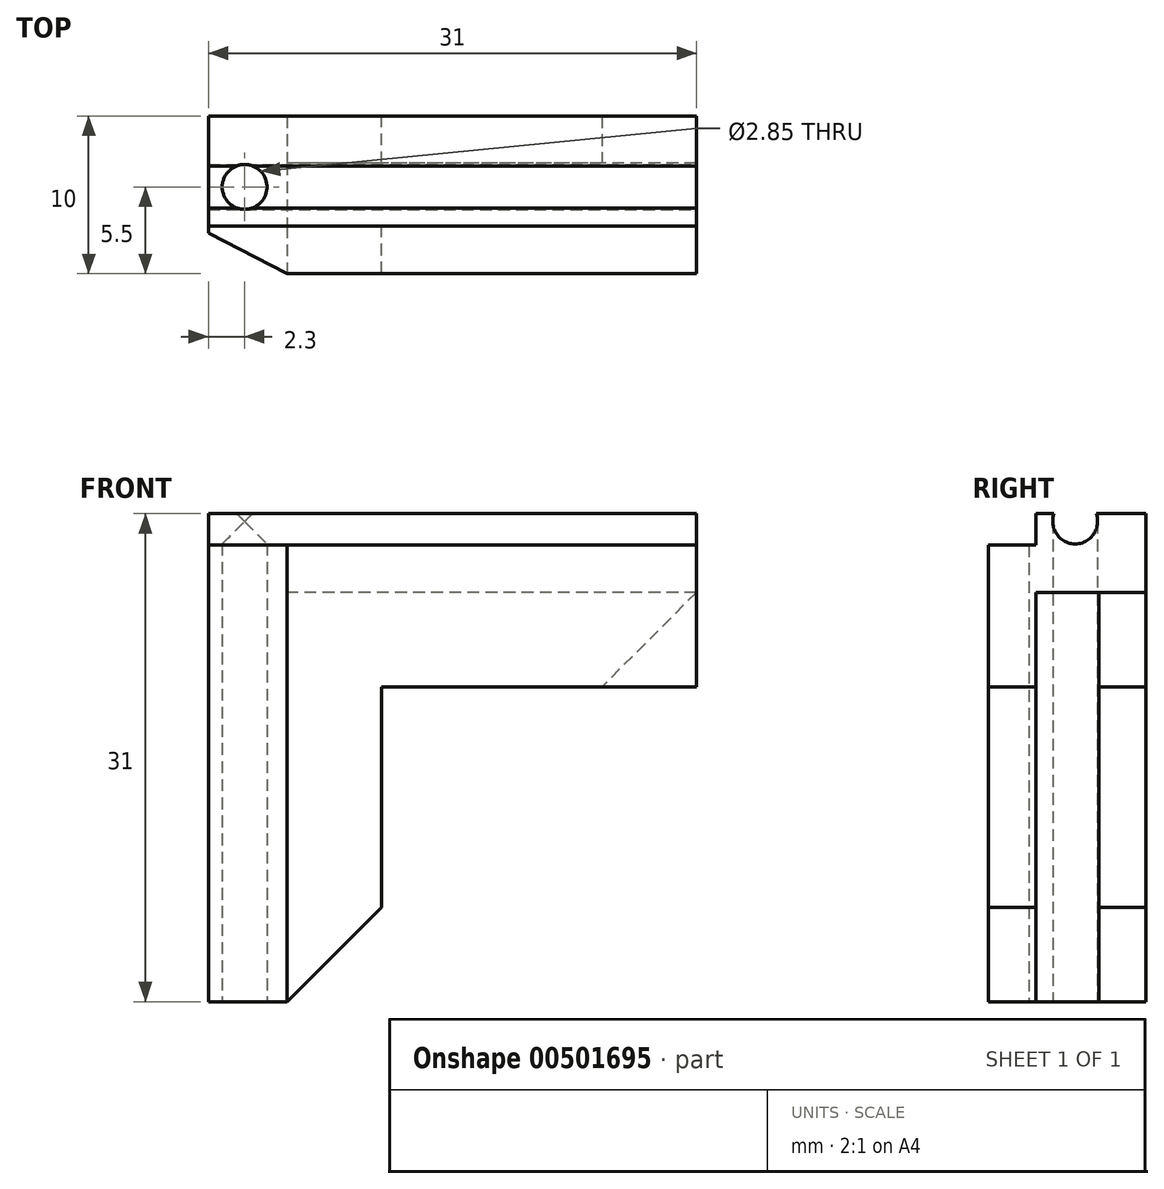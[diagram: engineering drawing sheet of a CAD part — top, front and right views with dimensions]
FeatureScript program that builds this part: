
annotation { "Feature Type Name" : "Feature", "Feature Type Description" : "" }
export const myFeature = defineFeature(function(context is Context, id is Id, definition is map)
    precondition{}
    {
        {
            var Q0;
            Q0=qCreatedBy(makeId("Top.planeOp"),FACE);
            var sketch = newSketch(context, id + "F0", { "sketchPlane" : qUnion([Q0])});
            skLineSegment(sketch, "E0", {"start": v(-12.16, 9.11) * mm, "end": v(-12.16, -0.89) * mm});
            skLineSegment(sketch, "E1", {"start": v(-12.16, -0.89) * mm, "end": v(-3.16, -0.89) * mm});
            skLineSegment(sketch, "E2", {"start": v(-3.16, -0.89) * mm, "end": v(-3.16, 2.11) * mm});
            skLineSegment(sketch, "E3", {"start": v(-3.16, 2.11) * mm, "end": v(-9.16, 2.11) * mm});
            skLineSegment(sketch, "E4", {"start": v(-9.16, 2.11) * mm, "end": v(-9.16, 6.11) * mm});
            skLineSegment(sketch, "E5", {"start": v(-9.16, 6.11) * mm, "end": v(-3.16, 6.11) * mm});
            skLineSegment(sketch, "E6", {"start": v(-3.16, 6.11) * mm, "end": v(-3.16, 9.11) * mm});
            skLineSegment(sketch, "E7", {"start": v(-3.16, 9.11) * mm, "end": v(-12.16, 9.11) * mm});
            skSolve(sketch);
        }
        {
            var Q0;
            Q0=makeQuery(id+"F0.imprint","IMPRINT",FACE,{"disambiguationData":[TD([[makeQuery(id+"F0.imprint","IMPRINT",EDGE,{"derivedFrom":sQuery(id+"F0.wireOp",EDGE,"E0")}),1.0]])]});
            extrude(context, id + "F1", {"entities" : qUnion([Q0]), "depth" : 20 * mm});
        }
        {
            var Q0;
            Q0=makeQuery(id+"F1.opExtrude","SWEPT_FACE",FACE,{"disambiguationData":[OSD([sQuery(id+"F0.wireOp",EDGE,"E0")])]});
            var sketch = newSketch(context, id + "F2", { "sketchPlane" : qUnion([Q0])});
            skLineSegment(sketch, "E8.bottom", {"start": v(-9.11, 20) * mm, "end": v(-2.11, 20) * mm});
            skLineSegment(sketch, "E8.top", {"start": v(-9.11, 0) * mm, "end": v(-2.11, 0) * mm});
            skLineSegment(sketch, "E8.left", {"start": v(-9.11, 20) * mm, "end": v(-9.11, 0) * mm});
            skLineSegment(sketch, "E8.right", {"start": v(-2.11, 20) * mm, "end": v(-2.11, 0) * mm});
            skSolve(sketch);
        }
        {
            var Q0;
            Q0=makeQuery(id+"F2.imprint","IMPRINT",FACE,{"disambiguationData":[TD([[makeQuery(id+"F2.imprint","IMPRINT",EDGE,{"derivedFrom":sQuery(id+"F2.wireOp",EDGE,"E8.bottom")}),-1.0]])]});
            extrude(context, id + "F3", {"entities" : qUnion([Q0]), "operationType" : NewBodyOperationType.ADD, "depth" : 2 * mm});
        }
        {
            var Q0;
            Q0=makeQuery(id+"F1.opExtrude","CAP_FACE",FACE,{"disambiguationData":[OSD([sQuery(id+"F0.wireOp",EDGE,"E0"),sQuery(id+"F0.wireOp",EDGE,"E1"),sQuery(id+"F0.wireOp",EDGE,"E2"),sQuery(id+"F0.wireOp",EDGE,"E3"),sQuery(id+"F0.wireOp",EDGE,"E4"),sQuery(id+"F0.wireOp",EDGE,"E5"),sQuery(id+"F0.wireOp",EDGE,"E6"),sQuery(id+"F0.wireOp",EDGE,"E7")])],"isStart":false});
            var sketch = newSketch(context, id + "F4", { "sketchPlane" : qUnion([Q0])});
            skLineSegment(sketch, "E9", {"start": v(-12.16, 2.11) * mm, "end": v(-12.13, 9.11) * mm});
            skLineSegment(sketch, "E10", {"start": v(-9.16, 9.11) * mm, "end": v(-9.16, -0.89) * mm});
            skSolve(sketch);
        }
        {
            var Q0;
            Q0=makeQuery(id+"F4.imprint","IMPRINT",FACE,{"disambiguationData":[TD([[makeQuery(id+"F4.imprint","IMPRINT",EDGE,{"derivedFrom":sQuery(id+"F4.wireOp",EDGE,"E9")}),-1.0]])]});
            extrude(context, id + "F5", {"entities" : qUnion([Q0]), "operationType" : NewBodyOperationType.ADD, "depth" : 6 * mm});
        }
        {
            var Q0;
            Q0=makeQuery(id+"F5.boolean.opBoolean","MERGE",FACE,{"derivedFrom":[makeQuery(id+"F1.opExtrude","SWEPT_FACE",FACE,{"disambiguationData":[OSD([sQuery(id+"F0.wireOp",EDGE,"E4")])]}),makeQuery(id+"F5.opExtrude","SWEPT_FACE",FACE,{"disambiguationData":[OSD([sQuery(id+"F4.wireOp",EDGE,"E10")])]})]});
            var sketch = newSketch(context, id + "F6", { "sketchPlane" : qUnion([Q0])});
            skLineSegment(sketch, "E11", {"start": v(2.11, 20) * mm, "end": v(2.11, 26) * mm});
            skLineSegment(sketch, "E12", {"start": v(6.11, 20) * mm, "end": v(6.11, 26) * mm});
            skLineSegment(sketch, "E13.bottom", {"start": v(-0.89, 26) * mm, "end": v(9.11, 26) * mm});
            skLineSegment(sketch, "E13.top", {"start": v(-0.89, 29) * mm, "end": v(9.11, 29) * mm});
            skLineSegment(sketch, "E13.left", {"start": v(-0.89, 26) * mm, "end": v(-0.89, 29) * mm});
            skLineSegment(sketch, "E13.right", {"start": v(9.11, 26) * mm, "end": v(9.11, 29) * mm});
            skSolve(sketch);
        }
        {
            var Q0;
            {var subQ0=sQuery(id+"F6.wireOp",EDGE,"E12");Q0=makeQuery(id+"F6.imprint","IMPRINT",FACE,{"disambiguationData":[TD([[makeQuery(id+"F6.imprint","IMPRINT",EDGE,{"derivedFrom":subQ0}),-1.0]])]});}
            var Q1;
            {var subQ0=sQuery(id+"F6.wireOp",EDGE,"E11");Q1=makeQuery(id+"F6.imprint","IMPRINT",FACE,{"disambiguationData":[TD([[makeQuery(id+"F6.imprint","IMPRINT",EDGE,{"derivedFrom":subQ0}),1.0]])]});}
            var Q2;
            Q2=makeQuery(id+"F6.imprint","IMPRINT",FACE,{"disambiguationData":[TD([[makeQuery(id+"F6.imprint","IMPRINT",EDGE,{"derivedFrom":sQuery(id+"F6.wireOp",EDGE,"E13.top")}),-1.0]])]});
            extrude(context, id + "F7", {"entities" : qUnion([Q0, Q1, Q2]), "depth" : 25 * mm});
        }
        {
            var Q0;
            Q0=makeQuery(id+"F5.opExtrude","CAP_FACE",FACE,{"disambiguationData":[OSD([sQuery(id+"F0.wireOp",EDGE,"E0"),sQuery(id+"F0.wireOp",EDGE,"E1"),sQuery(id+"F0.wireOp",EDGE,"E7"),sQuery(id+"F4.wireOp",EDGE,"E9"),sQuery(id+"F4.wireOp",EDGE,"E10")])],"isStart":false});
            extrude(context, id + "F8", {"entities" : qUnion([Q0]), "depth" : 3 * mm});
        }
        {
            var Q0;
            Q0=makeQuery(id+"F7.opExtrude","SWEPT_BODY",BODY,{"disambiguationData":[OSD([sQuery(id+"F0.wireOp",EDGE,"E1"),sQuery(id+"F0.wireOp",EDGE,"E7"),sQuery(id+"F4.wireOp",EDGE,"E10"),sQuery(id+"F6.wireOp",EDGE,"E11"),sQuery(id+"F6.wireOp",EDGE,"E12"),sQuery(id+"F6.wireOp",EDGE,"E13.bottom"),sQuery(id+"F6.wireOp",EDGE,"E13.top"),sQuery(id+"F6.wireOp",EDGE,"E13.left"),sQuery(id+"F6.wireOp",EDGE,"E13.right")])]});
            var Q1;
            Q1=makeQuery(id+"F8.opExtrude","SWEPT_BODY",BODY,{"disambiguationData":[OSD([sQuery(id+"F0.wireOp",EDGE,"E0"),sQuery(id+"F0.wireOp",EDGE,"E1"),sQuery(id+"F0.wireOp",EDGE,"E7"),sQuery(id+"F4.wireOp",EDGE,"E9"),sQuery(id+"F4.wireOp",EDGE,"E10")])]});
            booleanBodies(context, id + "F9", {"operationType" : BooleanOperationType.UNION, "tools" : qUnion([Q0, Q1])});
        }
        {
            var Q0;
            Q0=makeQuery(id+"F7.opExtrude","SWEPT_BODY",BODY,{"disambiguationData":[OSD([sQuery(id+"F0.wireOp",EDGE,"E1"),sQuery(id+"F0.wireOp",EDGE,"E7"),sQuery(id+"F4.wireOp",EDGE,"E10"),sQuery(id+"F6.wireOp",EDGE,"E11"),sQuery(id+"F6.wireOp",EDGE,"E12"),sQuery(id+"F6.wireOp",EDGE,"E13.bottom"),sQuery(id+"F6.wireOp",EDGE,"E13.top"),sQuery(id+"F6.wireOp",EDGE,"E13.left"),sQuery(id+"F6.wireOp",EDGE,"E13.right")])]});
            var Q1;
            Q1=makeQuery(id+"F1.opExtrude","SWEPT_BODY",BODY,{"disambiguationData":[OSD([sQuery(id+"F0.wireOp",EDGE,"E0"),sQuery(id+"F0.wireOp",EDGE,"E1"),sQuery(id+"F0.wireOp",EDGE,"E2"),sQuery(id+"F0.wireOp",EDGE,"E3"),sQuery(id+"F0.wireOp",EDGE,"E4"),sQuery(id+"F0.wireOp",EDGE,"E5"),sQuery(id+"F0.wireOp",EDGE,"E6"),sQuery(id+"F0.wireOp",EDGE,"E7")])]});
            booleanBodies(context, id + "F10", {"operationType" : BooleanOperationType.UNION, "tools" : qUnion([Q0, Q1])});
        }
        {
            var Q0;
            Q0=makeQuery(id+"F9.opBoolean","MERGE",FACE,{"derivedFrom":[makeQuery(id+"F7.opExtrude","SWEPT_FACE",FACE,{"disambiguationData":[OSD([sQuery(id+"F6.wireOp",EDGE,"E13.top")])]}),makeQuery(id+"F8.opExtrude","CAP_FACE",FACE,{"disambiguationData":[OSD([sQuery(id+"F0.wireOp",EDGE,"E0"),sQuery(id+"F0.wireOp",EDGE,"E1"),sQuery(id+"F0.wireOp",EDGE,"E7"),sQuery(id+"F4.wireOp",EDGE,"E9"),sQuery(id+"F4.wireOp",EDGE,"E10")])],"isStart":false})]});
            var sketch = newSketch(context, id + "F11", { "sketchPlane" : qUnion([Q0])});
            skLineSegment(sketch, "E14.bottom", {"start": v(-12.16, 2.11) * mm, "end": v(15.84, 2.11) * mm});
            skLineSegment(sketch, "E14.top", {"start": v(-12.16, 9.11) * mm, "end": v(15.84, 9.11) * mm});
            skLineSegment(sketch, "E14.left", {"start": v(-12.16, 2.11) * mm, "end": v(-12.16, 9.11) * mm});
            skLineSegment(sketch, "E14.right", {"start": v(15.84, 2.11) * mm, "end": v(15.84, 9.11) * mm});
            skSolve(sketch);
        }
        {
            var Q0;
            Q0=makeQuery(id+"F11.imprint","IMPRINT",FACE,{"disambiguationData":[TD([[makeQuery(id+"F11.imprint","IMPRINT",EDGE,{"derivedFrom":sQuery(id+"F11.wireOp",EDGE,"E14.bottom")}),1.0]])]});
            extrude(context, id + "F12", {"entities" : qUnion([Q0]), "operationType" : NewBodyOperationType.ADD, "depth" : 2 * mm});
        }
        {
            var Q0;
            Q0=makeQuery(id+"F4.imprint","IMPRINT",FACE,{"disambiguationData":[TD([[makeQuery(id+"F4.imprint","IMPRINT",EDGE,{"derivedFrom":sQuery(id+"F4.wireOp",EDGE,"E9")}),1.0]])]});
            extrude(context, id + "F13", {"entities" : qUnion([Q0]), "operationType" : NewBodyOperationType.ADD, "depth" : 11 * mm});
        }
        {
            var Q0;
            {var subQ0=sQuery(id+"F2.wireOp",EDGE,"E8.right");Q0=makeQuery(id+"F13.boolean.opBoolean","MERGE",EDGE,{"derivedFrom":[makeQuery(id+"F3.opExtrude","CAP_EDGE",EDGE,{"disambiguationData":[OSD([subQ0])],"isStart":true}),makeQuery(id+"F13.opExtrude","SWEPT_EDGE",EDGE,{"disambiguationData":[OSD([sQuery(id+"F0.wireOp",EDGE,"E0"),sQuery(id+"F2.wireOp",EDGE,"E8.bottom"),subQ0,sQuery(id+"F4.wireOp",EDGE,"E9")])]})]});}
            var Q1;
            Q1=makeQuery(id+"F12.opExtrude","CAP_EDGE",EDGE,{"disambiguationData":[OSD([sQuery(id+"F11.wireOp",EDGE,"E14.bottom")])],"isStart":true});
            chamfer(context, id + "F14", {"entities" : qUnion([Q0, Q1]), "width" : 4 * mm, "tangentPropagation" : true});
        }
        {
            var Q0;
            {var subQ0=sQuery(id+"F0.wireOp",EDGE,"E1");var subQ1=sQuery(id+"F2.wireOp",EDGE,"E8.right");Q0=makeQuery(id+"F14.opChamfer","BLEND_EDGE",EDGE,{"blendedFrom":[makeQuery(id+"F13.boolean.opBoolean","MERGE",EDGE,{"derivedFrom":[makeQuery(id+"F3.opExtrude","CAP_EDGE",EDGE,{"disambiguationData":[OSD([subQ1])],"isStart":true}),makeQuery(id+"F13.opExtrude","SWEPT_EDGE",EDGE,{"disambiguationData":[OSD([sQuery(id+"F0.wireOp",EDGE,"E0"),sQuery(id+"F2.wireOp",EDGE,"E8.bottom"),subQ1,sQuery(id+"F4.wireOp",EDGE,"E9")])]})]}),makeQuery(id+"F10.opBoolean","MERGE",FACE,{"derivedFrom":[makeQuery(id+"F5.boolean.opBoolean","MERGE",FACE,{"derivedFrom":[makeQuery(id+"F1.opExtrude","SWEPT_FACE",FACE,{"disambiguationData":[OSD([subQ0])]}),makeQuery(id+"F5.opExtrude","SWEPT_FACE",FACE,{"disambiguationData":[OSD([subQ0])]})]}),makeQuery(id+"F9.opBoolean","MERGE",FACE,{"derivedFrom":[makeQuery(id+"F7.opExtrude","SWEPT_FACE",FACE,{"disambiguationData":[OSD([subQ0,sQuery(id+"F4.wireOp",EDGE,"E10"),sQuery(id+"F6.wireOp",EDGE,"E13.left")])]}),makeQuery(id+"F8.opExtrude","SWEPT_FACE",FACE,{"disambiguationData":[OSD([subQ0])]})]})]})],"blendedInto":[makeQuery(id+"F10.opBoolean","MERGE",FACE,{"derivedFrom":[makeQuery(id+"F5.boolean.opBoolean","MERGE",FACE,{"derivedFrom":[makeQuery(id+"F1.opExtrude","SWEPT_FACE",FACE,{"disambiguationData":[OSD([subQ0])]}),makeQuery(id+"F5.opExtrude","SWEPT_FACE",FACE,{"disambiguationData":[OSD([subQ0])]})]}),makeQuery(id+"F9.opBoolean","MERGE",FACE,{"derivedFrom":[makeQuery(id+"F7.opExtrude","SWEPT_FACE",FACE,{"disambiguationData":[OSD([subQ0,sQuery(id+"F4.wireOp",EDGE,"E10"),sQuery(id+"F6.wireOp",EDGE,"E13.left")])]}),makeQuery(id+"F8.opExtrude","SWEPT_FACE",FACE,{"disambiguationData":[OSD([subQ0])]})]})]})]});}
            var Q1;
            {var subQ0=sQuery(id+"F0.wireOp",EDGE,"E1");Q1=makeQuery(id+"F14.opChamfer","BLEND_EDGE",EDGE,{"blendedFrom":[makeQuery(id+"F12.opExtrude","CAP_EDGE",EDGE,{"disambiguationData":[OSD([sQuery(id+"F11.wireOp",EDGE,"E14.bottom")])],"isStart":true}),makeQuery(id+"F10.opBoolean","MERGE",FACE,{"derivedFrom":[makeQuery(id+"F5.boolean.opBoolean","MERGE",FACE,{"derivedFrom":[makeQuery(id+"F1.opExtrude","SWEPT_FACE",FACE,{"disambiguationData":[OSD([subQ0])]}),makeQuery(id+"F5.opExtrude","SWEPT_FACE",FACE,{"disambiguationData":[OSD([subQ0])]})]}),makeQuery(id+"F9.opBoolean","MERGE",FACE,{"derivedFrom":[makeQuery(id+"F7.opExtrude","SWEPT_FACE",FACE,{"disambiguationData":[OSD([subQ0,sQuery(id+"F4.wireOp",EDGE,"E10"),sQuery(id+"F6.wireOp",EDGE,"E13.left")])]}),makeQuery(id+"F8.opExtrude","SWEPT_FACE",FACE,{"disambiguationData":[OSD([subQ0])]})]})]})],"blendedInto":[makeQuery(id+"F10.opBoolean","MERGE",FACE,{"derivedFrom":[makeQuery(id+"F5.boolean.opBoolean","MERGE",FACE,{"derivedFrom":[makeQuery(id+"F1.opExtrude","SWEPT_FACE",FACE,{"disambiguationData":[OSD([subQ0])]}),makeQuery(id+"F5.opExtrude","SWEPT_FACE",FACE,{"disambiguationData":[OSD([subQ0])]})]}),makeQuery(id+"F9.opBoolean","MERGE",FACE,{"derivedFrom":[makeQuery(id+"F7.opExtrude","SWEPT_FACE",FACE,{"disambiguationData":[OSD([subQ0,sQuery(id+"F4.wireOp",EDGE,"E10"),sQuery(id+"F6.wireOp",EDGE,"E13.left")])]}),makeQuery(id+"F8.opExtrude","SWEPT_FACE",FACE,{"disambiguationData":[OSD([subQ0])]})]})]})]});}
            chamfer(context, id + "F15", {"entities" : qUnion([Q0, Q1]), "chamferType" : ChamferType.TWO_OFFSETS, "width1" : 4 * mm, "oppositeDirection" : false, "width2" : 6 * mm, "tangentPropagation" : true});
        }
        {
            var Q0;
            Q0=makeQuery(id+"F12.boolean.opBoolean","MERGE",FACE,{"derivedFrom":[makeQuery(id+"F7.opExtrude","CAP_FACE",FACE,{"disambiguationData":[OSD([sQuery(id+"F0.wireOp",EDGE,"E1"),sQuery(id+"F0.wireOp",EDGE,"E7"),sQuery(id+"F4.wireOp",EDGE,"E10"),sQuery(id+"F6.wireOp",EDGE,"E11"),sQuery(id+"F6.wireOp",EDGE,"E12"),sQuery(id+"F6.wireOp",EDGE,"E13.bottom"),sQuery(id+"F6.wireOp",EDGE,"E13.top"),sQuery(id+"F6.wireOp",EDGE,"E13.left"),sQuery(id+"F6.wireOp",EDGE,"E13.right")])],"isStart":false}),makeQuery(id+"F12.opExtrude","SWEPT_FACE",FACE,{"disambiguationData":[OSD([sQuery(id+"F11.wireOp",EDGE,"E14.right")])]})]});
            extrude(context, id + "F16", {"entities" : qUnion([Q0]), "operationType" : NewBodyOperationType.ADD, "depth" : 1 * mm});
        }
        {
            var Q0;
            {var subQ2=sQuery(id+"F0.wireOp",EDGE,"E1");var subQ3=sQuery(id+"F4.wireOp",EDGE,"E10");Q0=makeQuery(id+"F16.opExtrude","CAP_EDGE",EDGE,{"disambiguationData":[OSD([subQ3]),TDD([makeQuery(id+"F7.opExtrude","CAP_EDGE",EDGE,{"disambiguationData":[OSD([subQ3]),TDD([makeQuery(id+"F6.imprint","IMPRINT",EDGE,{"derivedFrom":makeQuery(id+"F5.boolean.opBoolean","SPLIT",EDGE,{"disambiguationData":[TD([makeQuery(id+"F1.opExtrude","SWEPT_FACE",FACE,{"disambiguationData":[OSD([subQ2])]})])],"derivedFrom":makeQuery(id+"F5.opExtrude","CAP_EDGE",EDGE,{"disambiguationData":[OSD([subQ3])],"isStart":true})})})])],"isStart":false})])],"isStart":false});}
            var Q1;
            {var subQ1=sQuery(id+"F4.wireOp",EDGE,"E10");var subQ3=sQuery(id+"F0.wireOp",EDGE,"E5");Q1=makeQuery(id+"F16.opExtrude","CAP_EDGE",EDGE,{"disambiguationData":[OSD([subQ1]),TDD([makeQuery(id+"F7.opExtrude","CAP_EDGE",EDGE,{"disambiguationData":[OSD([subQ1]),TDD([makeQuery(id+"F6.imprint","IMPRINT",EDGE,{"derivedFrom":makeQuery(id+"F5.boolean.opBoolean","SPLIT",EDGE,{"disambiguationData":[TD([makeQuery(id+"F1.opExtrude","SWEPT_FACE",FACE,{"disambiguationData":[OSD([subQ3])]})])],"derivedFrom":makeQuery(id+"F5.opExtrude","CAP_EDGE",EDGE,{"disambiguationData":[OSD([subQ1])],"isStart":true})})})])],"isStart":false})])],"isStart":false});}
            var Q2;
            Q2=makeQuery(id+"F1.opExtrude","CAP_EDGE",EDGE,{"disambiguationData":[OSD([sQuery(id+"F0.wireOp",EDGE,"E2")])],"isStart":true});
            var Q3;
            Q3=makeQuery(id+"F1.opExtrude","CAP_EDGE",EDGE,{"disambiguationData":[OSD([sQuery(id+"F0.wireOp",EDGE,"E6")])],"isStart":true});
            chamfer(context, id + "F17", {"entities" : qUnion([Q0, Q1, Q2, Q3]), "width" : 6 * mm, "tangentPropagation" : true});
        }
        {
            var Q0;
            Q0=makeQuery(id+"F16.opExtrude","CAP_FACE",FACE,{"disambiguationData":[OSD([sQuery(id+"F0.wireOp",EDGE,"E1"),sQuery(id+"F0.wireOp",EDGE,"E7"),sQuery(id+"F2.wireOp",EDGE,"E8.bottom"),sQuery(id+"F2.wireOp",EDGE,"E8.left"),sQuery(id+"F4.wireOp",EDGE,"E10"),sQuery(id+"F6.wireOp",EDGE,"E11"),sQuery(id+"F6.wireOp",EDGE,"E12"),sQuery(id+"F6.wireOp",EDGE,"E13.bottom"),sQuery(id+"F6.wireOp",EDGE,"E13.top"),sQuery(id+"F6.wireOp",EDGE,"E13.left"),sQuery(id+"F6.wireOp",EDGE,"E13.right"),sQuery(id+"F11.wireOp",EDGE,"E14.right")])],"isStart":false});
            var sketch = newSketch(context, id + "F18", { "sketchPlane" : qUnion([Q0])});
            skPoint(sketch, "E15", {"position": v(4.61, 30.5) * mm});
            skSolve(sketch);
        }
        {
            var Q0;
            Q0=makeQuery(id+"F3.boolean.opBoolean","MERGE",FACE,{"derivedFrom":[makeQuery(id+"F1.opExtrude","CAP_FACE",FACE,{"disambiguationData":[OSD([sQuery(id+"F0.wireOp",EDGE,"E0"),sQuery(id+"F0.wireOp",EDGE,"E1"),sQuery(id+"F0.wireOp",EDGE,"E2"),sQuery(id+"F0.wireOp",EDGE,"E3"),sQuery(id+"F0.wireOp",EDGE,"E4"),sQuery(id+"F0.wireOp",EDGE,"E5"),sQuery(id+"F0.wireOp",EDGE,"E6"),sQuery(id+"F0.wireOp",EDGE,"E7")])],"isStart":true}),makeQuery(id+"F3.opExtrude","SWEPT_FACE",FACE,{"disambiguationData":[OSD([sQuery(id+"F2.wireOp",EDGE,"E8.top")])]})]});
            var sketch = newSketch(context, id + "F19", { "sketchPlane" : qUnion([Q0])});
            skPoint(sketch, "E16", {"position": v(-11.86, -4.61) * mm});
            skSolve(sketch);
        }
        {
            var Q0;
            Q0=sQuery(id+"F19.wireOp",VERTEX,"E16");
            var Q1;
            Q1=sQuery(id+"F18.wireOp",VERTEX,"E15");
            var Q2;
            Q2=makeQuery(id+"F7.opExtrude","SWEPT_BODY",BODY,{"disambiguationData":[OSD([sQuery(id+"F0.wireOp",EDGE,"E1"),sQuery(id+"F0.wireOp",EDGE,"E7"),sQuery(id+"F2.wireOp",EDGE,"E8.bottom"),sQuery(id+"F2.wireOp",EDGE,"E8.left"),sQuery(id+"F4.wireOp",EDGE,"E10"),sQuery(id+"F6.wireOp",EDGE,"E11"),sQuery(id+"F6.wireOp",EDGE,"E12"),sQuery(id+"F6.wireOp",EDGE,"E13.bottom"),sQuery(id+"F6.wireOp",EDGE,"E13.top"),sQuery(id+"F6.wireOp",EDGE,"E13.left"),sQuery(id+"F6.wireOp",EDGE,"E13.right")])]});
            hole(context, id + "F20", {"style" : HoleStyle.SIMPLE, "endStyle" : HoleEndStyle.THROUGH, "holeDiameter" : 2.85 * mm, "isTappedThrough" : true, "tappedDepth" : 12 * mm, "tapClearance" : 3, "locations" : qUnion([Q0, Q1]), "scope" : qUnion([Q2])});
        }
    });
